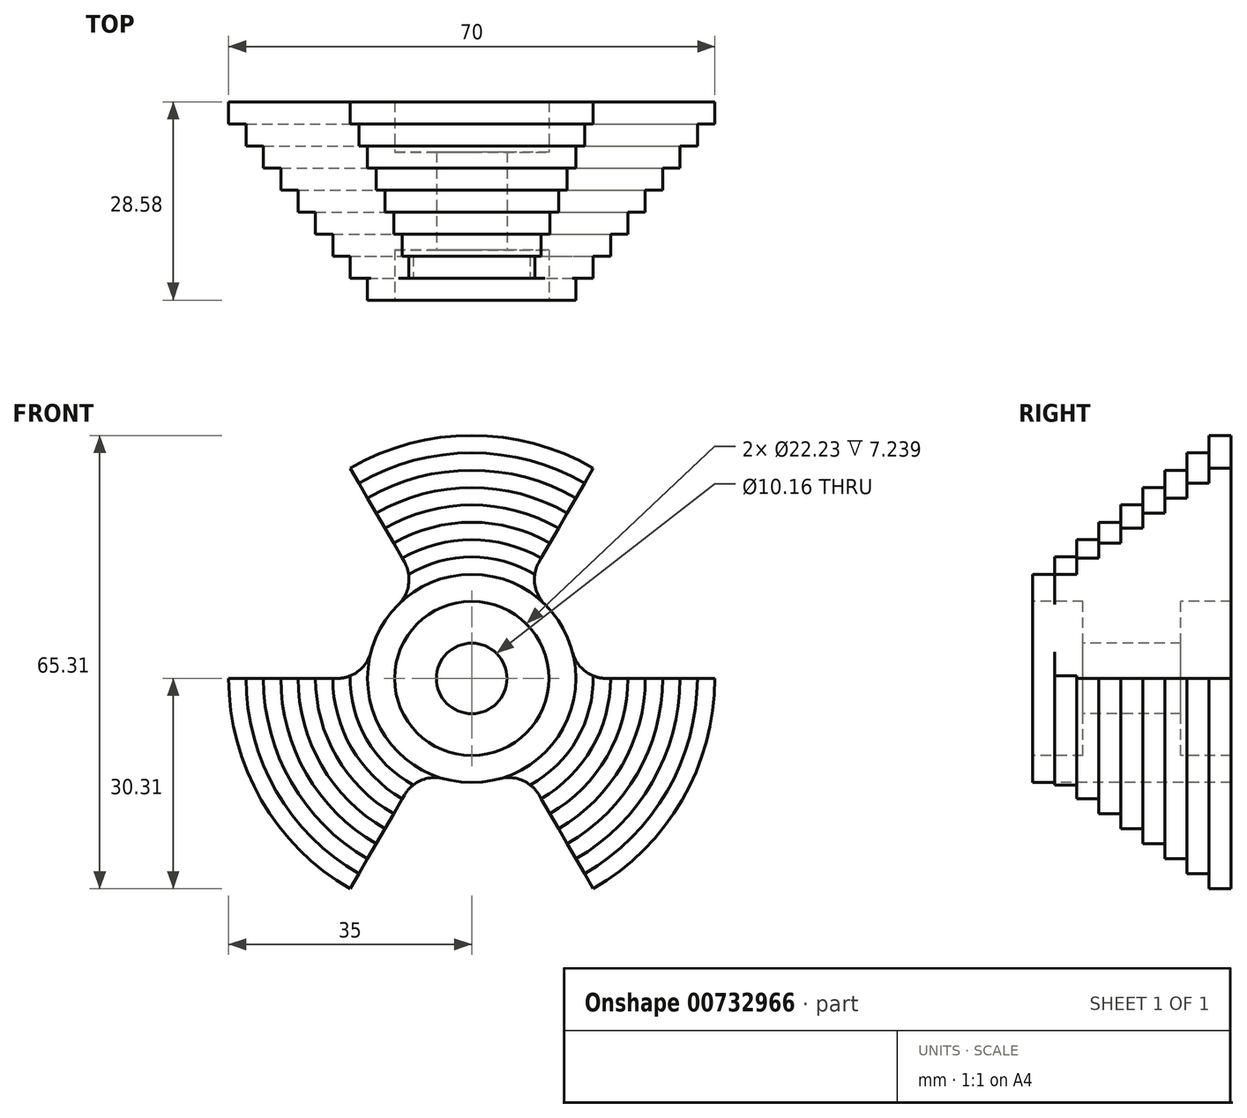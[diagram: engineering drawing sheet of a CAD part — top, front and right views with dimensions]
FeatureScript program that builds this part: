
annotation { "Feature Type Name" : "Feature", "Feature Type Description" : "" }
export const myFeature = defineFeature(function(context is Context, id is Id, definition is map)
    precondition{}
    {
        {
            var Q0;
            Q0=qCreatedBy(makeId("Right.planeOp"),FACE);
            var sketch = newSketch(context, id + "F0", { "sketchPlane" : qUnion([Q0])});
            skLineSegment(sketch, "E0", {"start": v(0, 0) * mm, "end": v(28.58, 0) * mm, "construction": true});
            skLineSegment(sketch, "E1", {"start": v(0, 11.11) * mm, "end": v(7.24, 11.11) * mm});
            skLineSegment(sketch, "E2", {"start": v(7.24, 11.11) * mm, "end": v(7.24, 5.08) * mm});
            skLineSegment(sketch, "E3", {"start": v(7.24, 5.08) * mm, "end": v(21.34, 5.08) * mm});
            skLineSegment(sketch, "E4", {"start": v(21.34, 5.08) * mm, "end": v(21.34, 11.11) * mm});
            skLineSegment(sketch, "E5", {"start": v(21.34, 11.11) * mm, "end": v(28.58, 11.11) * mm});
            skLineSegment(sketch, "E6", {"start": v(15.88, 25) * mm, "end": v(12.7, 25) * mm});
            skLineSegment(sketch, "E7", {"start": v(12.7, 25) * mm, "end": v(12.7, 22.5) * mm});
            skLineSegment(sketch, "E8", {"start": v(12.7, 22.5) * mm, "end": v(9.53, 22.5) * mm});
            skLineSegment(sketch, "E9", {"start": v(9.53, 22.5) * mm, "end": v(9.53, 20) * mm});
            skLineSegment(sketch, "E10", {"start": v(9.53, 20) * mm, "end": v(6.35, 20) * mm});
            skLineSegment(sketch, "E11", {"start": v(6.35, 20) * mm, "end": v(6.35, 17.5) * mm});
            skLineSegment(sketch, "E12", {"start": v(6.35, 17.5) * mm, "end": v(3.17, 17.5) * mm});
            skLineSegment(sketch, "E13", {"start": v(3.17, 17.5) * mm, "end": v(3.18, 15) * mm});
            skLineSegment(sketch, "E14", {"start": v(3.18, 15) * mm, "end": v(0, 15) * mm});
            skLineSegment(sketch, "E15", {"start": v(0, 15) * mm, "end": v(0, 11.11) * mm});
            skLineSegment(sketch, "E16", {"start": v(15.88, 25) * mm, "end": v(15.88, 27.5) * mm});
            skLineSegment(sketch, "E17", {"start": v(15.88, 27.5) * mm, "end": v(19.05, 27.5) * mm});
            skLineSegment(sketch, "E18", {"start": v(19.05, 27.5) * mm, "end": v(19.05, 30) * mm});
            skLineSegment(sketch, "E19", {"start": v(19.05, 30) * mm, "end": v(22.23, 30) * mm});
            skLineSegment(sketch, "E20", {"start": v(22.23, 30) * mm, "end": v(22.23, 32.5) * mm});
            skLineSegment(sketch, "E21", {"start": v(22.23, 32.5) * mm, "end": v(25.4, 32.5) * mm});
            skLineSegment(sketch, "E22", {"start": v(25.4, 32.5) * mm, "end": v(25.4, 35) * mm});
            skLineSegment(sketch, "E23", {"start": v(25.4, 35) * mm, "end": v(28.58, 35) * mm});
            skLineSegment(sketch, "E24", {"start": v(28.58, 35) * mm, "end": v(28.58, 11.11) * mm});
            skSolve(sketch);
        }
        {
            var Q0;
            Q0=makeQuery(id+"F0.imprint","IMPRINT",FACE,{"disambiguationData":[TD([[makeQuery(id+"F0.imprint","IMPRINT",EDGE,{"derivedFrom":sQuery(id+"F0.wireOp",EDGE,"E1")}),1.0]])]});
            var Q1;
            Q1=sQuery(id+"F0.wireOp",EDGE,"E0");
            revolve(context, id + "F1", {"surfaceOperationType" : NewSurfaceOperationType.NEW, "entities" : qUnion([Q0]), "axis" : qUnion([Q1]), "revolveType" : RevolveType.FULL});
        }
        {
            var Q0;
            Q0=qCreatedBy(makeId("Front.planeOp"),FACE);
            var sketch = newSketch(context, id + "F2", { "sketchPlane" : qUnion([Q0])});
            skCircle(sketch, "E25.0", {"center": v(0, 0) * mm, "radius": 15 * mm});
            skCircle(sketch, "E26.0", {"center": v(0, 0) * mm, "radius": 35 * mm});
            skLineSegment(sketch, "E27", {"start": v(7.5, 13) * mm, "end": v(17.5, 30.31) * mm});
            skLineSegment(sketch, "E28", {"start": v(-7.5, 13) * mm, "end": v(-17.5, 30.31) * mm});
            skLineSegment(sketch, "E29", {"start": v(-15, 0) * mm, "end": v(-35, 0) * mm});
            skLineSegment(sketch, "E30", {"start": v(-7.5, -13) * mm, "end": v(-17.5, -30.31) * mm});
            skLineSegment(sketch, "E31", {"start": v(7.5, -13) * mm, "end": v(17.5, -30.31) * mm});
            skLineSegment(sketch, "E32", {"start": v(15, 0) * mm, "end": v(35, 0) * mm});
            skSolve(sketch);
        }
        {
            var Q0;
            {var subQ0=sQuery(id+"F2.wireOp",EDGE,"E28");Q0=makeQuery(id+"F2.imprint","IMPRINT",FACE,{"disambiguationData":[TD([[makeQuery(id+"F2.imprint","IMPRINT",EDGE,{"derivedFrom":subQ0}),1.0]])]});}
            var Q1;
            {var subQ0=sQuery(id+"F2.wireOp",EDGE,"E27");Q1=makeQuery(id+"F2.imprint","IMPRINT",FACE,{"disambiguationData":[TD([[makeQuery(id+"F2.imprint","IMPRINT",EDGE,{"derivedFrom":subQ0}),-1.0]])]});}
            var Q2;
            {var subQ0=sQuery(id+"F2.wireOp",EDGE,"E30");Q2=makeQuery(id+"F2.imprint","IMPRINT",FACE,{"disambiguationData":[TD([[makeQuery(id+"F2.imprint","IMPRINT",EDGE,{"derivedFrom":subQ0}),1.0]])]});}
            extrude(context, id + "F3", {"entities" : qUnion([Q0, Q1, Q2]), "operationType" : NewBodyOperationType.REMOVE, "endBound" : BoundingType.THROUGH_ALL, "oppositeDirection" : true, "depth" : 25.4 * mm, "offsetDistance" : 25.4 * mm});
        }
        {
            var Q0;
            Q0=makeQuery(id+"F3.boolean.opBoolean","COPY",EDGE,{"derivedFrom":makeQuery(id+"F3.opExtrude","SWEPT_EDGE",EDGE,{"disambiguationData":[OSD([sQuery(id+"F2.wireOp",EDGE,"E25.0"),sQuery(id+"F2.wireOp",EDGE,"E32")])]})});
            var Q1;
            Q1=makeQuery(id+"F3.boolean.opBoolean","COPY",EDGE,{"derivedFrom":makeQuery(id+"F3.opExtrude","SWEPT_EDGE",EDGE,{"disambiguationData":[OSD([sQuery(id+"F2.wireOp",EDGE,"E25.0"),sQuery(id+"F2.wireOp",EDGE,"E27")])]})});
            var Q2;
            Q2=makeQuery(id+"F3.boolean.opBoolean","COPY",EDGE,{"derivedFrom":makeQuery(id+"F3.opExtrude","SWEPT_EDGE",EDGE,{"disambiguationData":[OSD([sQuery(id+"F2.wireOp",EDGE,"E25.0"),sQuery(id+"F2.wireOp",EDGE,"E28")])]})});
            var Q3;
            Q3=makeQuery(id+"F3.boolean.opBoolean","COPY",EDGE,{"derivedFrom":makeQuery(id+"F3.opExtrude","SWEPT_EDGE",EDGE,{"disambiguationData":[OSD([sQuery(id+"F2.wireOp",EDGE,"E25.0"),sQuery(id+"F2.wireOp",EDGE,"E29")])]})});
            var Q4;
            Q4=makeQuery(id+"F3.boolean.opBoolean","COPY",EDGE,{"derivedFrom":makeQuery(id+"F3.opExtrude","SWEPT_EDGE",EDGE,{"disambiguationData":[OSD([sQuery(id+"F2.wireOp",EDGE,"E25.0"),sQuery(id+"F2.wireOp",EDGE,"E30")])]})});
            var Q5;
            Q5=makeQuery(id+"F3.boolean.opBoolean","COPY",EDGE,{"derivedFrom":makeQuery(id+"F3.opExtrude","SWEPT_EDGE",EDGE,{"disambiguationData":[OSD([sQuery(id+"F2.wireOp",EDGE,"E25.0"),sQuery(id+"F2.wireOp",EDGE,"E31")])]})});
            fillet(context, id + "F4", {"entities" : qUnion([Q0, Q1, Q2, Q3, Q4, Q5]), "radius" : 5.08 * mm, "tangentPropagation" : true, "allowEdgeOverflow" : false});
        }
    });
